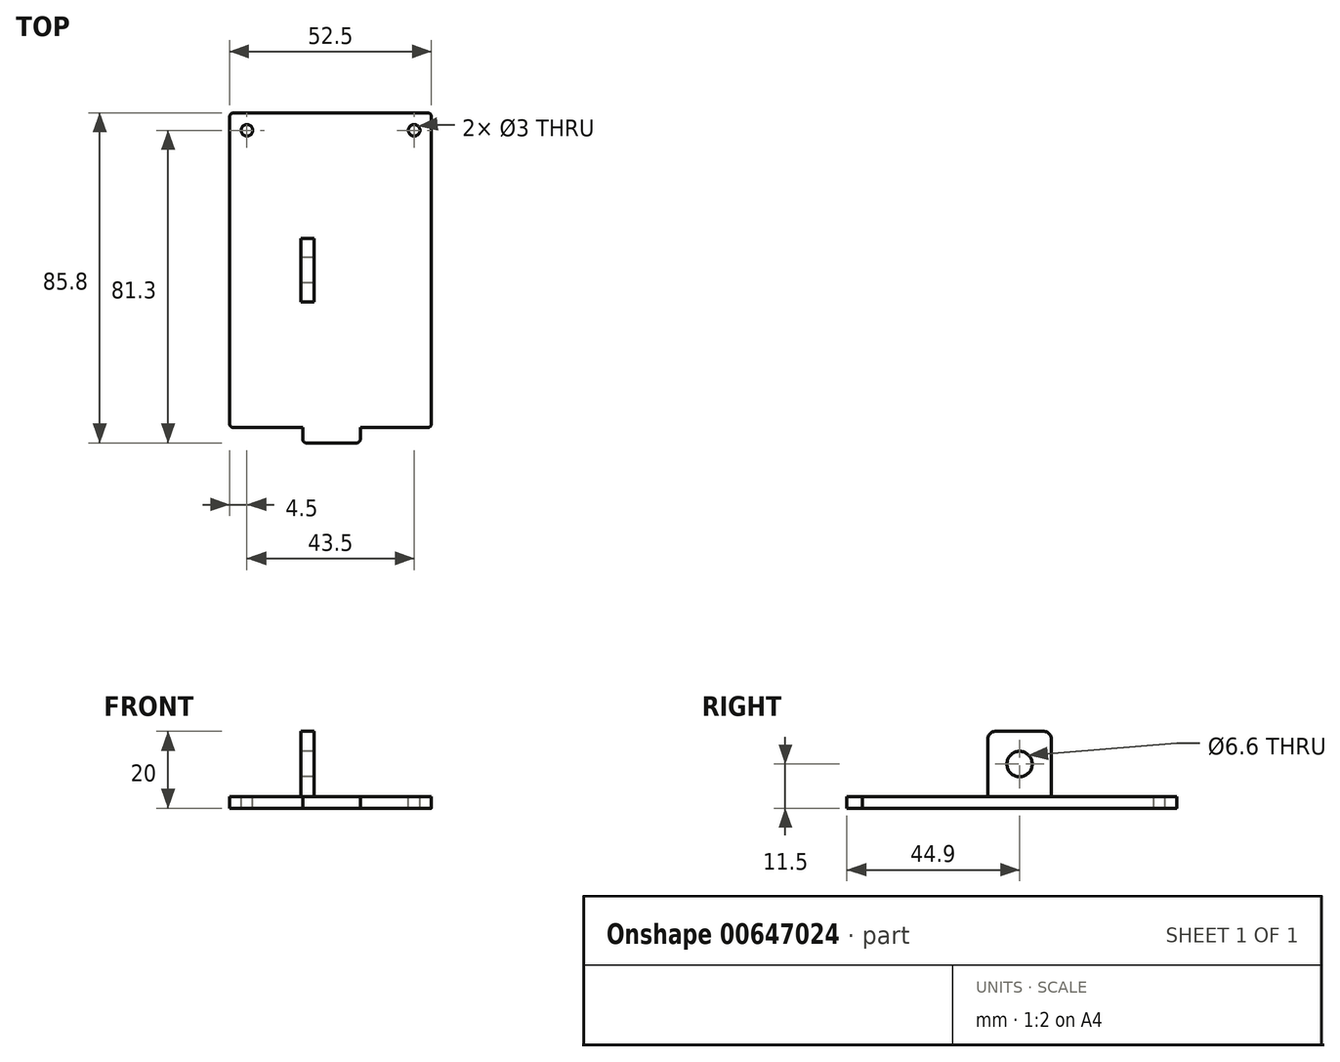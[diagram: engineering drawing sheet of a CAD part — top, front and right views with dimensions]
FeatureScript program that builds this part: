
annotation { "Feature Type Name" : "Feature", "Feature Type Description" : "" }
export const myFeature = defineFeature(function(context is Context, id is Id, definition is map)
    precondition{}
    {
        {
            var Q0;
            Q0=qCreatedBy(makeId("Top.planeOp"),FACE);
            var sketch = newSketch(context, id + "F0", { "sketchPlane" : qUnion([Q0])});
            skLineSegment(sketch, "E0.bottom", {"start": v(1, 0) * mm, "end": v(51.5, 0) * mm});
            skLineSegment(sketch, "E0.top", {"start": v(1, -81.8) * mm, "end": v(51.5, -81.8) * mm});
            skLineSegment(sketch, "E0.left", {"start": v(0, -1) * mm, "end": v(0, -80.8) * mm});
            skLineSegment(sketch, "E0.right", {"start": v(52.5, -1) * mm, "end": v(52.5, -80.8) * mm});
            skLineSegment(sketch, "E1.bottom", {"start": v(33, -85.8) * mm, "end": v(20, -85.8) * mm});
            skLineSegment(sketch, "E1.left", {"start": v(34, -84.8) * mm, "end": v(34, -81.8) * mm});
            skLineSegment(sketch, "E1.right", {"start": v(19, -84.8) * mm, "end": v(19, -81.8) * mm});
            skPoint(sketch, "E1.middle", {"position": v(26.25, -85.8) * mm});
            skPoint(sketch, "E2.visualSharp", {"position": v(19, -85.8) * mm});
            skArc(sketch, "E2.filletArc", {"start": v(19, -84.8) * mm, "mid": v(19.29, -85.5) * mm, "end": v(20, -85.8) * mm});
            skPoint(sketch, "E3.visualSharp", {"position": v(34, -85.8) * mm});
            skArc(sketch, "E3.filletArc", {"start": v(33, -85.8) * mm, "mid": v(33.7, -85.5) * mm, "end": v(34, -84.8) * mm});
            skPoint(sketch, "E4.visualSharp", {"position": v(0, -81.8) * mm});
            skArc(sketch, "E4.filletArc", {"start": v(0, -80.8) * mm, "mid": v(0.3, -81.5) * mm, "end": v(1, -81.8) * mm});
            skPoint(sketch, "E5.visualSharp", {"position": v(52.5, -81.8) * mm});
            skArc(sketch, "E5.filletArc", {"start": v(51.5, -81.8) * mm, "mid": v(52.2, -81.5) * mm, "end": v(52.5, -80.8) * mm});
            skPoint(sketch, "E6.visualSharp", {"position": v(52.5, 0) * mm});
            skArc(sketch, "E6.filletArc", {"start": v(52.5, -1) * mm, "mid": v(52.2, -0.3) * mm, "end": v(51.5, 0) * mm});
            skPoint(sketch, "E7.visualSharp", {"position": v(0, 0) * mm});
            skArc(sketch, "E7.filletArc", {"start": v(1, 0) * mm, "mid": v(0.3, -0.3) * mm, "end": v(0, -1) * mm});
            skLineSegment(sketch, "E8", {"start": v(26.25, 0) * mm, "end": v(26.25, -85.8) * mm});
            skLineSegment(sketch, "E9", {"start": v(52.5, -40.9) * mm, "end": v(0, -40.9) * mm});
            skCircle(sketch, "E10", {"center": v(48, -4.5) * mm, "radius": 1.5 * mm});
            skCircle(sketch, "E11", {"center": v(4.5, -4.5) * mm, "radius": 1.5 * mm});
            skSolve(sketch);
        }
        {
            var Q0;
            Q0 = qSketchRegion(id + "F0", true);
            extrude(context, id + "F1", {"entities" : qUnion([Q0]), "oppositeDirection" : true, "depth" : 3 * mm, "offsetDistance" : 25.4 * mm});
        }
        {
            var Q0;
            Q0=qCreatedBy(makeId("Right.planeOp"),FACE);
            var sketch = newSketch(context, id + "F2", { "sketchPlane" : qUnion([Q0])});
            skLineSegment(sketch, "E12", {"start": v(-49.15, 0) * mm, "end": v(-49.15, 17) * mm});
            skLineSegment(sketch, "E13", {"start": v(-49.15, 17) * mm, "end": v(-32.65, 17) * mm});
            skLineSegment(sketch, "E14", {"start": v(-32.65, 17) * mm, "end": v(-32.65, 0) * mm});
            skCircle(sketch, "E15", {"center": v(-40.9, 8.5) * mm, "radius": 3.3 * mm});
            skPoint(sketch, "E16", {"position": v(-40.9, 0) * mm});
            skLineSegment(sketch, "E17", {"start": v(-49.15, 0) * mm, "end": v(-32.65, 0) * mm});
            skSolve(sketch);
        }
        {
            var Q0;
            Q0=makeQuery(id+"F2.imprint","IMPRINT",FACE,{"disambiguationData":[TD([[makeQuery(id+"F2.imprint","IMPRINT",EDGE,{"derivedFrom":sQuery(id+"F2.wireOp",EDGE,"E12")}),-1.0]])]});
            extrude(context, id + "F3", {"entities" : qUnion([Q0]), "operationType" : NewBodyOperationType.ADD, "depth" : 22 * mm, "offsetDistance" : 25.4 * mm, "hasSecondDirection" : true, "secondDirectionOppositeDirection" : false, "secondDirectionDepth" : 18.5 * mm});
        }
        {
            var Q0;
            Q0=makeQuery(id+"F3.opExtrude","SWEPT_EDGE",EDGE,{"disambiguationData":[OSD([sQuery(id+"F2.wireOp",EDGE,"E12"),sQuery(id+"F2.wireOp",EDGE,"E13")])]});
            var Q1;
            Q1=makeQuery(id+"F3.opExtrude","SWEPT_EDGE",EDGE,{"disambiguationData":[OSD([sQuery(id+"F2.wireOp",EDGE,"E13"),sQuery(id+"F2.wireOp",EDGE,"E14")])]});
            fillet(context, id + "F4", {"entities" : qUnion([Q0, Q1]), "radius" : 2 * mm, "tangentPropagation" : true, "allowEdgeOverflow" : false});
        }
    });
